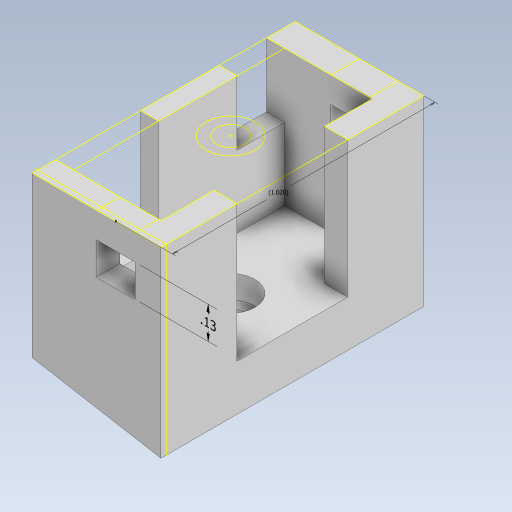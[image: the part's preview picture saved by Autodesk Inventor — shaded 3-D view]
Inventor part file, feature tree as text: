
AUTODESK INVENTOR PART (.ipt)
format: ipt  version: 2024 (Build 280153000, 153)  size: 593,920 bytes
history: native  units: in
note: dims shown in document units (in); Inventor stores cm internally (conversion verified against a paired STEP export)
features: projected_geometry x31, sketch x9, thicken_offset x9, extrude x5, other x2, hole x1
ambient origin geometry x8: Origin, YZ Plane, XZ Plane, XY Plane, X Axis, Y Axis, Z Axis, Center Point
bodies: Body1 (feature_tree)
feature tree (57):
  other  "Annotations"
  extrude  "Extrusion9"  Depth=0.32in
  sketch  "Sketch10"  dims[d31=0.05in d32=0.05in]
  extrude  "Extrusion10"  Depth=0.05in
  extrude  "Extrusion11"  Depth=0.225in
  extrude  "Extrusion12"  Depth=0.53in
  hole  "Hole1"  [1 undecoded]
  thicken_offset  "Thicken2"
  thicken_offset  "Thicken3"
  thicken_offset  "Thicken4"
  thicken_offset  "Thicken5"
  thicken_offset  "Thicken6"
  thicken_offset  "Thicken7"
  thicken_offset  "Thicken8"
  sketch  "Sketch15"  dims[d45=1.3056in]
  thicken_offset  "Thicken9"
  thicken_offset  "Thicken10"
  extrude  "Extrusion13"  Depth=1.0in TaperAngle=0.0deg
  sketch  "Sketch17"  dims[d48=0.1in d49=1.1681in d50=0.11in d51=0.75in d52=0.19in d53=0.09in d54=0.5635in d55=1.0in d56=0.0in d57=0.05in d58=0.05in d59=0.03in d60=0.03in d61=0.05in d62=0.05in d63=0.04in d64=0.04in d65=0.04in d66=0.04in d67=0.02in d68=0.02in d69=0.02in d70=0.02in d71=0.02in d72=0.02in d73=0.02in d74=0.02in d75=0.1in d76=0.1in d77=0.125in d78=0.15in d79=2.0in d80=0.0in d81=1.02in d82=0.2856in d83=0.1893in d84=0.125in]
  sketch  "Sketch9"  dims[d29=0.32in d30=0.78in]
  sketch  "Sketch11"  dims[d33=0.53in d34=0.0in d35=0.225in]
  sketch  "Sketch12"  dims[d36=0.53in d37=0.0in d38=0.3in]
  sketch  "Sketch13"  dims[d39=180.0deg d40=0.42in]
  sketch  "Sketch14"  dims[d41=90.0deg d42=1.0in d43=0.0in]
  sketch  "Sketch16"  dims[d46=1.0in d47=0.0in]
  projected_geometry  "Projected Loop1"
  projected_geometry  "Projected Loop2"
  projected_geometry  "Projected Loop3"
  projected_geometry  "Projected Loop4"
  projected_geometry  "Projected Loop5"
  projected_geometry  "Projected Loop6"
  projected_geometry  "Projected Loop7"
  projected_geometry  "Projected Loop8"
  projected_geometry  "Projected Loop9"
  projected_geometry  "Projected Loop10"
  projected_geometry  "Projected Loop11"
  projected_geometry  "Projected Loop12"
  projected_geometry  "Projected Loop13"
  projected_geometry  "Projected Loop14"
  projected_geometry  "Projected Loop15"
  projected_geometry  "Projected Loop16"
  projected_geometry  "Projected Loop17"
  projected_geometry  "Projected Loop18"
  projected_geometry  "Projected Loop19"
  projected_geometry  "Projected Loop20"
  projected_geometry  "Projected Loop21"
  projected_geometry  "Projected Loop22"
  projected_geometry  "Projected Loop23"
  projected_geometry  "Projected Loop24"
  projected_geometry  "Projected Loop25"
  projected_geometry  "Projected Loop26"
  projected_geometry  "Projected Loop27"
  projected_geometry  "Projected Loop28"
  projected_geometry  "Projected Loop29"
  projected_geometry  "Projected Loop30"
  projected_geometry  "Projected Loop31"
  other  "Linear Dimension 1"
note: 1 required parameter value undecoded (feature->parameter linkage not recoverable at this tier; creation-order binding heuristic only, values carry confidence <= 0.55)
